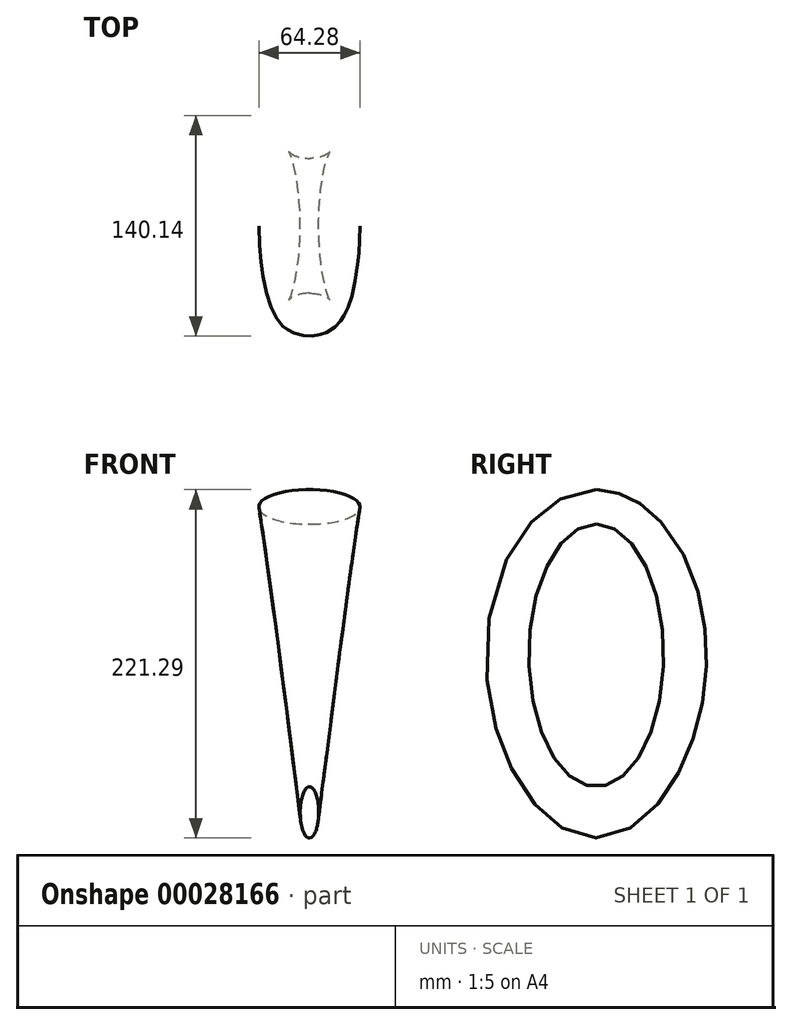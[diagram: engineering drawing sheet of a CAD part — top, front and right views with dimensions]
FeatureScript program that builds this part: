
annotation { "Feature Type Name" : "Feature", "Feature Type Description" : "" }
export const myFeature = defineFeature(function(context is Context, id is Id, definition is map)
    precondition{}
    {
        {
            var Q0;
            Q0=qCreatedBy(makeId("Right.planeOp"),FACE);
            var sketch = newSketch(context, id + "F0", { "sketchPlane" : qUnion([Q0])});
            skEllipse(sketch, "E0", {"center": v(0, 0) * mm, "majorRadius": 83.37 * mm, "minorRadius": 42.8 * mm, "majorAxis": v(0, 1)});
            skSolve(sketch);
        }
        {
            var Q0;
            Q0=qCreatedBy(makeId("Front.planeOp"),FACE);
            var sketch = newSketch(context, id + "F1", { "sketchPlane" : qUnion([Q0])});
            skEllipse(sketch, "E1", {"center": v(0, 94.36) * mm, "majorRadius": 32.14 * mm, "minorRadius": 10.98 * mm, "majorAxis": v(1, 0)});
            skEllipse(sketch, "E2", {"center": v(0, -99.66) * mm, "majorRadius": 16.29 * mm, "minorRadius": 5.87 * mm, "majorAxis": v(0, -1)});
            skPoint(sketch, "E3", {"position": v(0, 83.37) * mm});
            skPoint(sketch, "E4", {"position": v(0, -83.37) * mm});
            skSolve(sketch);
        }
        {
            var Q0;
            Q0=makeQuery(id+"F1.imprint","IMPRINT",FACE,{"disambiguationData":[TD([[makeQuery(id+"F1.imprint","IMPRINT",EDGE,{"derivedFrom":sQuery(id+"F1.wireOp",EDGE,"E1")}),1.0]])]});
            var Q1;
            Q1=makeQuery(id+"F1.imprint","IMPRINT",FACE,{"disambiguationData":[TD([[makeQuery(id+"F1.imprint","IMPRINT",EDGE,{"derivedFrom":sQuery(id+"F1.wireOp",EDGE,"E2")}),1.0]])]});
            var Q2;
            Q2=sQuery(id+"F1.wireOp",EDGE,"E1");
            var Q3;
            Q3=sQuery(id+"F1.wireOp",EDGE,"E2");
            var Q4;
            Q4=sQuery(id+"F0.wireOp",EDGE,"E0");
            loft(context, id + "F2", {"bodyType" : ToolBodyType.SURFACE, "addGuides" : true, "sheetProfilesArray" : [{ "sheetProfileEntities" : qUnion([Q0]) }, { "sheetProfileEntities" : qUnion([Q1]) }], "wireProfilesArray" : [{ "wireProfileEntities" : qUnion([Q2]) }, { "wireProfileEntities" : qUnion([Q3]) }], "guidesArray" : [{ "guideEntities" : qUnion([Q4]), "guideDerivativeType" : LoftGuideDerivativeType.DEFAULT, "guideDerivativeMagnitude" : 1 }]});
        }
    });
